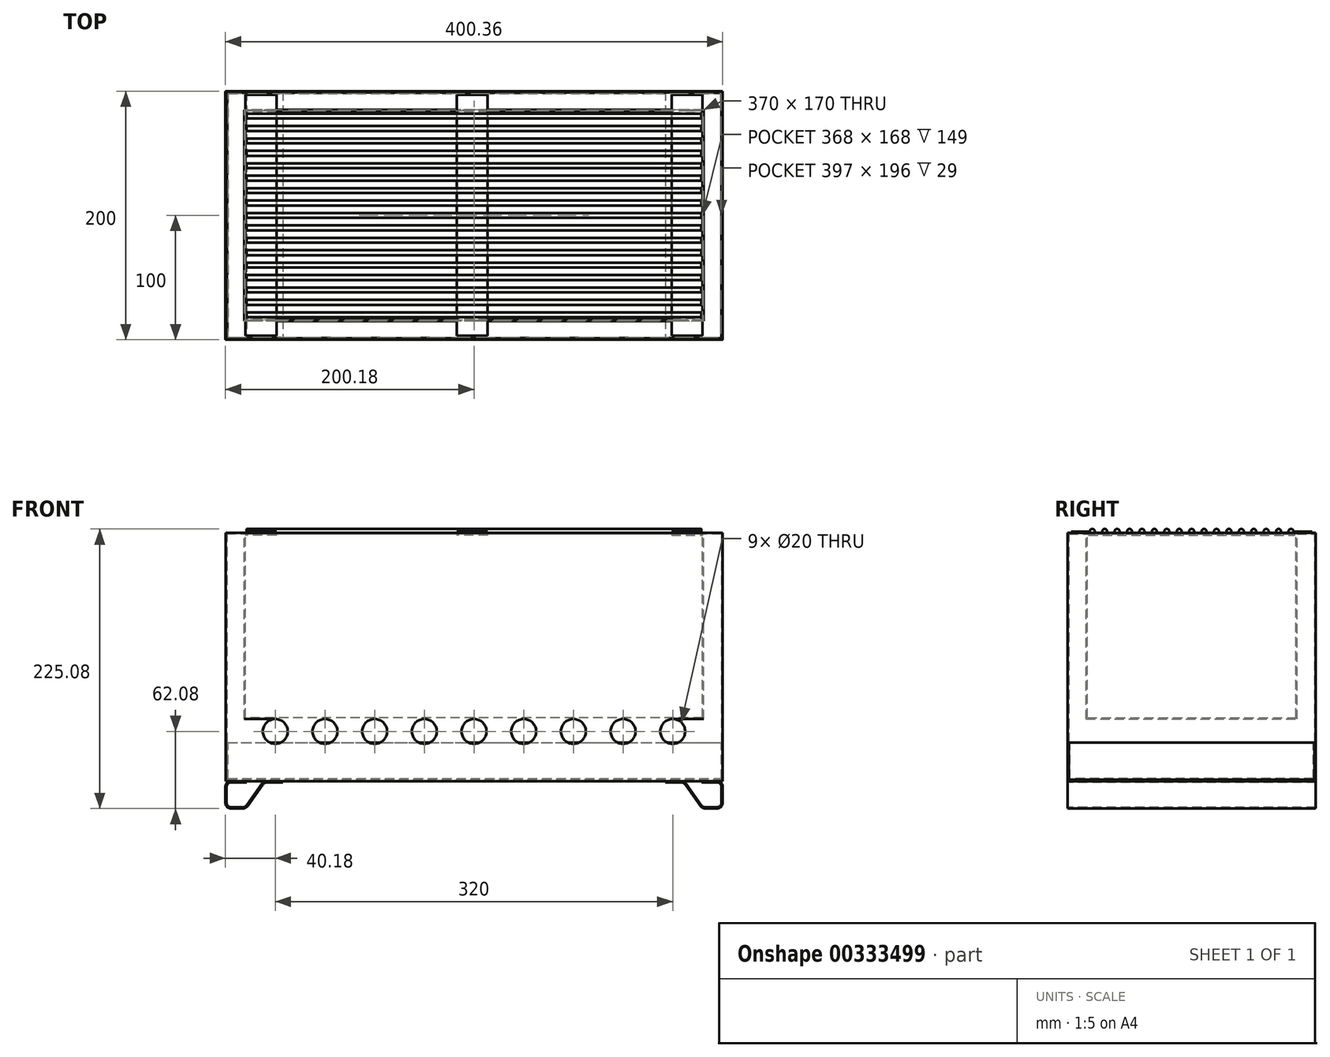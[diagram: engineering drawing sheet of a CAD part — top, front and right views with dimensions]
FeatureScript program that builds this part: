
annotation { "Feature Type Name" : "Feature", "Feature Type Description" : "" }
export const myFeature = defineFeature(function(context is Context, id is Id, definition is map)
    precondition{}
    {
        {
            assignVariable(context, id + "F0", {"name" : "Width", "anyValue" : 400});
        }
        {
            assignVariable(context, id + "F1", {"name" : "Depth", "anyValue" : 200});
        }
        {
            assignVariable(context, id + "F2", {"name" : "Height", "anyValue" : 200});
        }
        {
            var Q0;
            Q0=qCreatedBy(makeId("Top.planeOp"),FACE);
            var sketch = newSketch(context, id + "F3", { "sketchPlane" : qUnion([Q0])});
            skLineSegment(sketch, "E0.bottom", {"start": v(200, -100) * mm, "end": v(-200, -100) * mm});
            skLineSegment(sketch, "E0.top", {"start": v(200, 100) * mm, "end": v(-200, 100) * mm});
            skLineSegment(sketch, "E0.left", {"start": v(200, -100) * mm, "end": v(200, 100) * mm});
            skLineSegment(sketch, "E0.right", {"start": v(-200, -100) * mm, "end": v(-200, 100) * mm});
            skPoint(sketch, "E0.middle", {"position": v(0, 0) * mm});
            skSolve(sketch);
        }
        {
            var Q0;
            Q0 = qSketchRegion(id + "F3", true);
            extrude(context, id + "F4", {"entities" : qUnion([Q0]), "depth" : (getVariable(context, 'Height')) * mm});
        }
        {
            var Q0;
            Q0=makeQuery(id+"F4.opExtrude","CAP_FACE",FACE,{"disambiguationData":[OSD([sQuery(id+"F3.wireOp",EDGE,"E0.bottom"),sQuery(id+"F3.wireOp",EDGE,"E0.top"),sQuery(id+"F3.wireOp",EDGE,"E0.left"),sQuery(id+"F3.wireOp",EDGE,"E0.right")])],"isStart":false});
            shell(context, id + "F5", {"entities" : qUnion([Q0]), "thickness" : 1 * mm});
        }
        {
            var Q0;
            Q0=makeQuery(id+"F4.opExtrude","CAP_FACE",FACE,{"disambiguationData":[OSD([sQuery(id+"F3.wireOp",EDGE,"E0.bottom"),sQuery(id+"F3.wireOp",EDGE,"E0.top"),sQuery(id+"F3.wireOp",EDGE,"E0.left"),sQuery(id+"F3.wireOp",EDGE,"E0.right")])],"isStart":false});
            var sketch = newSketch(context, id + "F6", { "sketchPlane" : qUnion([Q0])});
            skLineSegment(sketch, "E1.bottom", {"start": v(185, -85) * mm, "end": v(-185, -85) * mm});
            skLineSegment(sketch, "E1.top", {"start": v(185, 85) * mm, "end": v(-185, 85) * mm});
            skLineSegment(sketch, "E1.left", {"start": v(185, -85) * mm, "end": v(185, 85) * mm});
            skLineSegment(sketch, "E1.right", {"start": v(-185, -85) * mm, "end": v(-185, 85) * mm});
            skPoint(sketch, "E1.middle", {"position": v(0, 0) * mm});
            skSolve(sketch);
        }
        {
            var Q0;
            Q0 = qSketchRegion(id + "F6", true);
            extrude(context, id + "F7", {"entities" : qUnion([Q0]), "oppositeDirection" : true, "depth" : (getVariable(context, 'Height') - 50) * mm});
        }
        {
            var Q0;
            Q0=makeQuery(id+"F7.opExtrude","CAP_FACE",FACE,{"disambiguationData":[OSD([sQuery(id+"F6.wireOp",EDGE,"E1.bottom"),sQuery(id+"F6.wireOp",EDGE,"E1.top"),sQuery(id+"F6.wireOp",EDGE,"E1.left"),sQuery(id+"F6.wireOp",EDGE,"E1.right")])],"isStart":true});
            shell(context, id + "F8", {"entities" : qUnion([Q0]), "thickness" : 1 * mm});
        }
        {
            var Q0;
            Q0=makeQuery(id+"F4.opExtrude","CAP_FACE",FACE,{"disambiguationData":[OSD([sQuery(id+"F3.wireOp",EDGE,"E0.bottom"),sQuery(id+"F3.wireOp",EDGE,"E0.top"),sQuery(id+"F3.wireOp",EDGE,"E0.left"),sQuery(id+"F3.wireOp",EDGE,"E0.right")])],"isStart":false});
            var sketch = newSketch(context, id + "F9", { "sketchPlane" : qUnion([Q0])});
            skLineSegment(sketch, "E2.0", {"start": v(185, -85) * mm, "end": v(-185, -85) * mm});
            skLineSegment(sketch, "E3.0", {"start": v(-185, -85) * mm, "end": v(-185, 85) * mm});
            skLineSegment(sketch, "E4.0", {"start": v(-199, -99) * mm, "end": v(-199, 99) * mm});
            skLineSegment(sketch, "E5.0", {"start": v(199, -99) * mm, "end": v(-199, -99) * mm});
            skLineSegment(sketch, "E6.0", {"start": v(185, -85) * mm, "end": v(185, 85) * mm});
            skLineSegment(sketch, "E7.0", {"start": v(185, 85) * mm, "end": v(-185, 85) * mm});
            skLineSegment(sketch, "E8.0", {"start": v(199, 99) * mm, "end": v(-199, 99) * mm});
            skLineSegment(sketch, "E9.0", {"start": v(199, -99) * mm, "end": v(199, 99) * mm});
            skSolve(sketch);
        }
        {
            var Q0;
            Q0 = qSketchRegion(id + "F9", true);
            extrude(context, id + "F10", {"entities" : qUnion([Q0]), "oppositeDirection" : true, "depth" : 1 * mm});
        }
        {
            var Q0;
            Q0=makeQuery(id+"F4.opExtrude","SWEPT_FACE",FACE,{"disambiguationData":[OSD([sQuery(id+"F3.wireOp",EDGE,"E0.left")])]});
            var sketch = newSketch(context, id + "F11", { "sketchPlane" : qUnion([Q0])});
            skLineSegment(sketch, "E10.bottom", {"start": v(99, 1) * mm, "end": v(-99, 1) * mm});
            skLineSegment(sketch, "E10.top", {"start": v(99, 31) * mm, "end": v(-99, 31) * mm});
            skLineSegment(sketch, "E10.left", {"start": v(99, 1) * mm, "end": v(99, 31) * mm});
            skLineSegment(sketch, "E10.right", {"start": v(-99, 1) * mm, "end": v(-99, 31) * mm});
            skPoint(sketch, "E10.middle", {"position": v(0, 16) * mm});
            skSolve(sketch);
        }
        {
            var Q0;
            Q0 = qSketchRegion(id + "F11", true);
            extrude(context, id + "F12", {"entities" : qUnion([Q0]), "operationType" : NewBodyOperationType.REMOVE, "oppositeDirection" : true, "depth" : 25 * mm});
        }
        {
            var Q0;
            Q0=makeQuery(id+"F4.opExtrude","SWEPT_FACE",FACE,{"disambiguationData":[OSD([sQuery(id+"F3.wireOp",EDGE,"E0.left")])]});
            var sketch = newSketch(context, id + "F13", { "sketchPlane" : qUnion([Q0])});
            skLineSegment(sketch, "E11.0", {"start": v(-99, 1) * mm, "end": v(-99, 31) * mm});
            skLineSegment(sketch, "E12.0", {"start": v(99, 31) * mm, "end": v(-99, 31) * mm});
            skLineSegment(sketch, "E13.0", {"start": v(99, 1) * mm, "end": v(-99, 1) * mm});
            skLineSegment(sketch, "E14.0", {"start": v(99, 1) * mm, "end": v(99, 31) * mm});
            skSolve(sketch);
        }
        {
            var Q0;
            Q0 = qSketchRegion(id + "F13", true);
            extrude(context, id + "F14", {"entities" : qUnion([Q0]), "oppositeDirection" : true, "depth" : (getVariable(context, 'Width') - 1) * mm});
        }
        {
            var Q0;
            Q0=makeQuery(id+"F14.opExtrude","SWEPT_FACE",FACE,{"disambiguationData":[OSD([sQuery(id+"F13.wireOp",EDGE,"E12.0")])]});
            shell(context, id + "F15", {"entities" : qUnion([Q0]), "thickness" : 1 * mm});
        }
        {
            var Q0;
            Q0=makeQuery(id+"F4.opExtrude","SWEPT_FACE",FACE,{"disambiguationData":[OSD([sQuery(id+"F3.wireOp",EDGE,"E0.bottom")])]});
            var sketch = newSketch(context, id + "F16", { "sketchPlane" : qUnion([Q0])});
            skCircle(sketch, "E15", {"center": v(-160, 40) * mm, "radius": 10 * mm});
            skCircle(sketch, "E16.1.0.0", {"center": v(-120, 40) * mm, "radius": 10 * mm});
            skCircle(sketch, "E16.2.0.0", {"center": v(-80, 40) * mm, "radius": 10 * mm});
            skCircle(sketch, "E16.3.0.0", {"center": v(-40, 40) * mm, "radius": 10 * mm});
            skCircle(sketch, "E16.4.0.0", {"center": v(0, 40) * mm, "radius": 10 * mm});
            skCircle(sketch, "E16.5.0.0", {"center": v(40, 40) * mm, "radius": 10 * mm});
            skCircle(sketch, "E16.6.0.0", {"center": v(80, 40) * mm, "radius": 10 * mm});
            skCircle(sketch, "E16.7.0.0", {"center": v(120, 40) * mm, "radius": 10 * mm});
            skCircle(sketch, "E16.8.0.0", {"center": v(160, 40) * mm, "radius": 10 * mm});
            skLineSegment(sketch, "E16.direction1", {"start": v(-160, 40) * mm, "end": v(-120, 40) * mm, "construction": true});
            skSolve(sketch);
        }
        {
            var Q0;
            Q0 = qSketchRegion(id + "F16", true);
            extrude(context, id + "F17", {"entities" : qUnion([Q0]), "operationType" : NewBodyOperationType.REMOVE, "oppositeDirection" : true, "depth" : 25 * mm});
        }
        {
            var Q0;
            Q0=makeQuery(id+"F8.opShell","OFFSET_FACE",FACE,{"disambiguationData":[OSD([sQuery(id+"F6.wireOp",EDGE,"E1.right")])]});
            var sketch = newSketch(context, id + "F18", { "sketchPlane" : qUnion([Q0])});
            skLineSegment(sketch, "E17", {"start": v(-97, 200) * mm, "end": v(-83, 200) * mm});
            skLineSegment(sketch, "E18", {"start": v(-83, 200) * mm, "end": v(-83, 198) * mm});
            skLineSegment(sketch, "E19", {"start": v(-83, 198) * mm, "end": v(83, 198) * mm});
            skLineSegment(sketch, "E20", {"start": v(83, 198) * mm, "end": v(83, 200) * mm});
            skLineSegment(sketch, "E21", {"start": v(83, 200) * mm, "end": v(97, 200) * mm});
            skLineSegment(sketch, "E22", {"start": v(97, 200) * mm, "end": v(97, 201) * mm});
            skLineSegment(sketch, "E23", {"start": v(82, 201) * mm, "end": v(82, 199) * mm});
            skLineSegment(sketch, "E24", {"start": v(82, 199) * mm, "end": v(-82, 199) * mm});
            skLineSegment(sketch, "E25", {"start": v(-82, 199) * mm, "end": v(-82, 201) * mm});
            skLineSegment(sketch, "E26", {"start": v(-82, 201) * mm, "end": v(-97, 201) * mm});
            skLineSegment(sketch, "E27", {"start": v(-97, 201) * mm, "end": v(-97, 200) * mm});
            skLineSegment(sketch, "E28", {"start": v(82, 201) * mm, "end": v(97, 201) * mm});
            skSolve(sketch);
        }
        {
            var Q0;
            Q0 = qSketchRegion(id + "F18", true);
            extrude(context, id + "F19", {"entities" : qUnion([Q0]), "depth" : 25 * mm});
        }
        {
            var Q0;
            Q0=makeQuery(id+"F19.opExtrude","SWEPT_BODY",BODY,{"disambiguationData":[OSD([sQuery(id+"F18.wireOp",EDGE,"E17"),sQuery(id+"F18.wireOp",EDGE,"E18"),sQuery(id+"F18.wireOp",EDGE,"E19"),sQuery(id+"F18.wireOp",EDGE,"E20"),sQuery(id+"F18.wireOp",EDGE,"E21"),sQuery(id+"F18.wireOp",EDGE,"E22"),sQuery(id+"F18.wireOp",EDGE,"E23"),sQuery(id+"F18.wireOp",EDGE,"E24"),sQuery(id+"F18.wireOp",EDGE,"E25"),sQuery(id+"F18.wireOp",EDGE,"E26"),sQuery(id+"F18.wireOp",EDGE,"E27"),sQuery(id+"F18.wireOp",EDGE,"E28")])]});
            var Q1;
            Q1=qCreatedBy(makeId("Right.planeOp"),FACE);
            mirror(context, id + "F20", {"entities" : qUnion([Q0]), "mirrorPlane" : qUnion([Q1])});
        }
        {
            var Q0;
            Q0=makeQuery(id+"F19.opExtrude","SWEPT_BODY",BODY,{"disambiguationData":[OSD([sQuery(id+"F18.wireOp",EDGE,"E17"),sQuery(id+"F18.wireOp",EDGE,"E18"),sQuery(id+"F18.wireOp",EDGE,"E19"),sQuery(id+"F18.wireOp",EDGE,"E20"),sQuery(id+"F18.wireOp",EDGE,"E21"),sQuery(id+"F18.wireOp",EDGE,"E22"),sQuery(id+"F18.wireOp",EDGE,"E23"),sQuery(id+"F18.wireOp",EDGE,"E24"),sQuery(id+"F18.wireOp",EDGE,"E25"),sQuery(id+"F18.wireOp",EDGE,"E26"),sQuery(id+"F18.wireOp",EDGE,"E27"),sQuery(id+"F18.wireOp",EDGE,"E28")])]});
            var Q1;
            Q1=makeQuery(id+"F7.opExtrude","CAP_EDGE",EDGE,{"disambiguationData":[OSD([sQuery(id+"F6.wireOp",EDGE,"E1.bottom")])],"isStart":true});
            transform(context, id + "F21", {"entities" : qUnion([Q0]), "transformType" : TransformType.TRANSLATION_DISTANCE, "transformDirection" : qUnion([Q1]), "distance" : 170 * mm, "oppositeDirection" : true, "makeCopy" : true});
        }
        {
            var Q0;
            Q0=qCreatedBy(makeId("Right.planeOp"),FACE);
            var sketch = newSketch(context, id + "F22", { "sketchPlane" : qUnion([Q0])});
            skCircle(sketch, "E29", {"center": v(-80, 201) * mm, "radius": 2 * mm});
            skCircle(sketch, "E30.1.0.0", {"center": v(-70, 201) * mm, "radius": 2 * mm});
            skCircle(sketch, "E30.2.0.0", {"center": v(-60, 201) * mm, "radius": 2 * mm});
            skCircle(sketch, "E30.3.0.0", {"center": v(-50, 201) * mm, "radius": 2 * mm});
            skCircle(sketch, "E30.4.0.0", {"center": v(-40, 201) * mm, "radius": 2 * mm});
            skCircle(sketch, "E30.5.0.0", {"center": v(-30, 201) * mm, "radius": 2 * mm});
            skCircle(sketch, "E30.6.0.0", {"center": v(-20, 201) * mm, "radius": 2 * mm});
            skCircle(sketch, "E30.7.0.0", {"center": v(-10, 201) * mm, "radius": 2 * mm});
            skCircle(sketch, "E30.8.0.0", {"center": v(0, 201) * mm, "radius": 2 * mm});
            skCircle(sketch, "E30.9.0.0", {"center": v(10, 201) * mm, "radius": 2 * mm});
            skCircle(sketch, "E30.10.0.0", {"center": v(20, 201) * mm, "radius": 2 * mm});
            skCircle(sketch, "E30.11.0.0", {"center": v(30, 201) * mm, "radius": 2 * mm});
            skCircle(sketch, "E30.12.0.0", {"center": v(40, 201) * mm, "radius": 2 * mm});
            skCircle(sketch, "E30.13.0.0", {"center": v(50, 201) * mm, "radius": 2 * mm});
            skCircle(sketch, "E30.14.0.0", {"center": v(60, 201) * mm, "radius": 2 * mm});
            skCircle(sketch, "E30.15.0.0", {"center": v(70, 201) * mm, "radius": 2 * mm});
            skCircle(sketch, "E30.16.0.0", {"center": v(80, 201) * mm, "radius": 2 * mm});
            skLineSegment(sketch, "E30.direction1", {"start": v(-80, 201) * mm, "end": v(-70, 201) * mm, "construction": true});
            skSolve(sketch);
        }
        {
            var Q0;
            Q0 = qSketchRegion(id + "F22", true);
            extrude(context, id + "F23", {"entities" : qUnion([Q0]), "depth" : 366 * mm, "symmetric" : true});
        }
        {
            var Q0;
            Q0=makeQuery(id+"F4.opExtrude","SWEPT_FACE",FACE,{"disambiguationData":[OSD([sQuery(id+"F3.wireOp",EDGE,"E0.bottom")])]});
            var sketch = newSketch(context, id + "F24", { "sketchPlane" : qUnion([Q0])});
            skLineSegment(sketch, "E31", {"start": v(-183.23, -1) * mm, "end": v(-195.62, -1) * mm});
            skLineSegment(sketch, "E32", {"start": v(-199.18, -4.55) * mm, "end": v(-199.18, -17.53) * mm});
            skLineSegment(sketch, "E33", {"start": v(-195.62, -21.08) * mm, "end": v(-186.28, -21.08) * mm});
            skLineSegment(sketch, "E34", {"start": v(-183.03, -19.4) * mm, "end": v(-170.94, -2.4) * mm});
            skLineSegment(sketch, "E35", {"start": v(-166.3, 0) * mm, "end": v(-153.91, 0) * mm});
            skArc(sketch, "E36", {"start": v(-195.62, -1) * mm, "mid": v(-198.14, -2.04) * mm, "end": v(-199.18, -4.55) * mm});
            skArc(sketch, "E37", {"start": v(-199.18, -17.53) * mm, "mid": v(-198.14, -20.04) * mm, "end": v(-195.62, -21.08) * mm});
            skArc(sketch, "E38", {"start": v(-186.28, -21.08) * mm, "mid": v(-184.45, -20.64) * mm, "end": v(-183.03, -19.4) * mm});
            skArc(sketch, "E39", {"start": v(-166.3, 0) * mm, "mid": v(-168.91, -0.63) * mm, "end": v(-170.94, -2.4) * mm});
            skLineSegment(sketch, "E40.0", {"start": v(-166.3, -1) * mm, "end": v(-153.91, -1) * mm});
            skArc(sketch, "E40.1", {"start": v(-166.3, -1) * mm, "mid": v(-168.45, -1.52) * mm, "end": v(-170.12, -2.97) * mm});
            skLineSegment(sketch, "E40.2", {"start": v(-182.21, -19.98) * mm, "end": v(-170.12, -2.97) * mm});
            skArc(sketch, "E40.3", {"start": v(-186.28, -22.08) * mm, "mid": v(-184, -21.52) * mm, "end": v(-182.21, -19.98) * mm});
            skLineSegment(sketch, "E40.4", {"start": v(-195.62, -22.08) * mm, "end": v(-186.28, -22.08) * mm});
            skLineSegment(sketch, "E40.5", {"start": v(-183.23, 0) * mm, "end": v(-195.62, 0) * mm});
            skArc(sketch, "E40.6", {"start": v(-195.62, 0) * mm, "mid": v(-198.84, -1.33) * mm, "end": v(-200.18, -4.55) * mm});
            skLineSegment(sketch, "E40.7", {"start": v(-200.18, -4.55) * mm, "end": v(-200.18, -17.53) * mm});
            skArc(sketch, "E40.8", {"start": v(-200.18, -17.53) * mm, "mid": v(-198.84, -20.75) * mm, "end": v(-195.62, -22.08) * mm});
            skLineSegment(sketch, "E41", {"start": v(-183.23, -1) * mm, "end": v(-183.23, 0) * mm});
            skLineSegment(sketch, "E42", {"start": v(-153.91, -1) * mm, "end": v(-153.91, 0) * mm});
            skSolve(sketch);
        }
        {
            var Q0;
            Q0 = qSketchRegion(id + "F24", true);
            extrude(context, id + "F25", {"entities" : qUnion([Q0]), "oppositeDirection" : true, "depth" : (getVariable(context, 'Depth')) * mm});
        }
        {
            var Q0;
            Q0=makeQuery(id+"F25.opExtrude","SWEPT_BODY",BODY,{"disambiguationData":[OSD([sQuery(id+"F24.wireOp",EDGE,"E31"),sQuery(id+"F24.wireOp",EDGE,"E32"),sQuery(id+"F24.wireOp",EDGE,"E33"),sQuery(id+"F24.wireOp",EDGE,"E34"),sQuery(id+"F24.wireOp",EDGE,"E35"),sQuery(id+"F24.wireOp",EDGE,"E36"),sQuery(id+"F24.wireOp",EDGE,"E37"),sQuery(id+"F24.wireOp",EDGE,"E38"),sQuery(id+"F24.wireOp",EDGE,"E39"),sQuery(id+"F24.wireOp",EDGE,"E40.0"),sQuery(id+"F24.wireOp",EDGE,"E40.1"),sQuery(id+"F24.wireOp",EDGE,"E40.2"),sQuery(id+"F24.wireOp",EDGE,"E40.3"),sQuery(id+"F24.wireOp",EDGE,"E40.4"),sQuery(id+"F24.wireOp",EDGE,"E40.5"),sQuery(id+"F24.wireOp",EDGE,"E40.6"),sQuery(id+"F24.wireOp",EDGE,"E40.7"),sQuery(id+"F24.wireOp",EDGE,"E40.8"),sQuery(id+"F24.wireOp",EDGE,"E41"),sQuery(id+"F24.wireOp",EDGE,"E42")])]});
            var Q1;
            Q1=qCreatedBy(makeId("Right.planeOp"),FACE);
            mirror(context, id + "F26", {"entities" : qUnion([Q0]), "mirrorPlane" : qUnion([Q1])});
        }
    });
